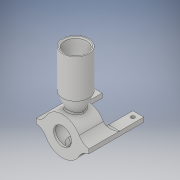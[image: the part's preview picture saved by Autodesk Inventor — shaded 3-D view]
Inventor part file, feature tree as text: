
AUTODESK INVENTOR PART (.ipt)
format: ipt  version: 2017 (Build 210142000, 142)  size: 327,168 bytes
history: native  units: in
note: dims shown in document units (in); Inventor stores cm internally (conversion verified against a paired STEP export)
features: sketch x8, extrude x5, fillet x5, plane x2, hole x2, revolve x1, chamfer x1, projected_geometry x1
ambient origin geometry x8: Origin, YZ Plane, XZ Plane, XY Plane, X Axis, Y Axis, Z Axis, Center Point
bodies: Solid1 (feature_tree)
feature tree (25):
  extrude  "Extrusion1"  Depth=0.25in
  extrude  "Extrusion2"  Depth=0.2in
  plane  "Work Plane1"
  hole  "Hole1"  [1 undecoded]
  plane  "Work Plane2"
  revolve  "Revolution1"  [1 undecoded]
  extrude  "Extrusion3"  TaperAngle=90.0deg  [1 undecoded]
  fillet  "Fillet1"  Radius=1.75in
  fillet  "Fillet2"  Radius=0.05in
  extrude  "Extrusion5"  Depth=0.05in
  chamfer  "Chamfer2"  Distance=1.0in
  extrude  "Extrusion6"  Depth=0.05in
  fillet  "Fillet3"  Radius=0.7in
  hole  "Hole2"  [1 undecoded]
  fillet  "Fillet4"  Radius=0.2in
  fillet  "Fillet5"  Radius=0.6in
  sketch  "Sketch1"  dims[d0=1.22in d1=0.25in]
  sketch  "Sketch2"  dims[d2=1.0in d3=0.0in d4=0.2in]
  sketch  "Sketch3"  dims[d5=0.1in d6=0.0in]
  sketch  "Sketch4"  dims[d7=0.35in d8=0.75in d9=0.375in d10=0.25in d11=0.5635in d12=0.5in d13=0.8108in d14=-0.5in]
  sketch  "Sketch5"  dims[d15=0.1in d16=1.5in]
  projected_geometry  "Projected Loop1"
  sketch  "Sketch7"  dims[d18=0.1in d19=90.0deg d20=1.75in d21=0.0in d22=0.05in]
  sketch  "Sketch8"  dims[d23=0.05in d30=0.05in d31=1.0in d32=0.0in]
  sketch  "Sketch9"  dims[d33=0.125in d34=0.125in d35=45.0deg d36=0.5in d37=0.7in d38=2.5in d39=0.2in d40=0.0in d41=0.6in d42=0.1667in d43=0.75in d44=0.375in d45=0.25in d46=0.5635in d47=0.5in d48=0.8108in d49=0.3in d50=0.05in d51=0.6in]
note: 4 required parameter values undecoded (feature->parameter linkage not recoverable at this tier; creation-order binding heuristic only, values carry confidence <= 0.55)